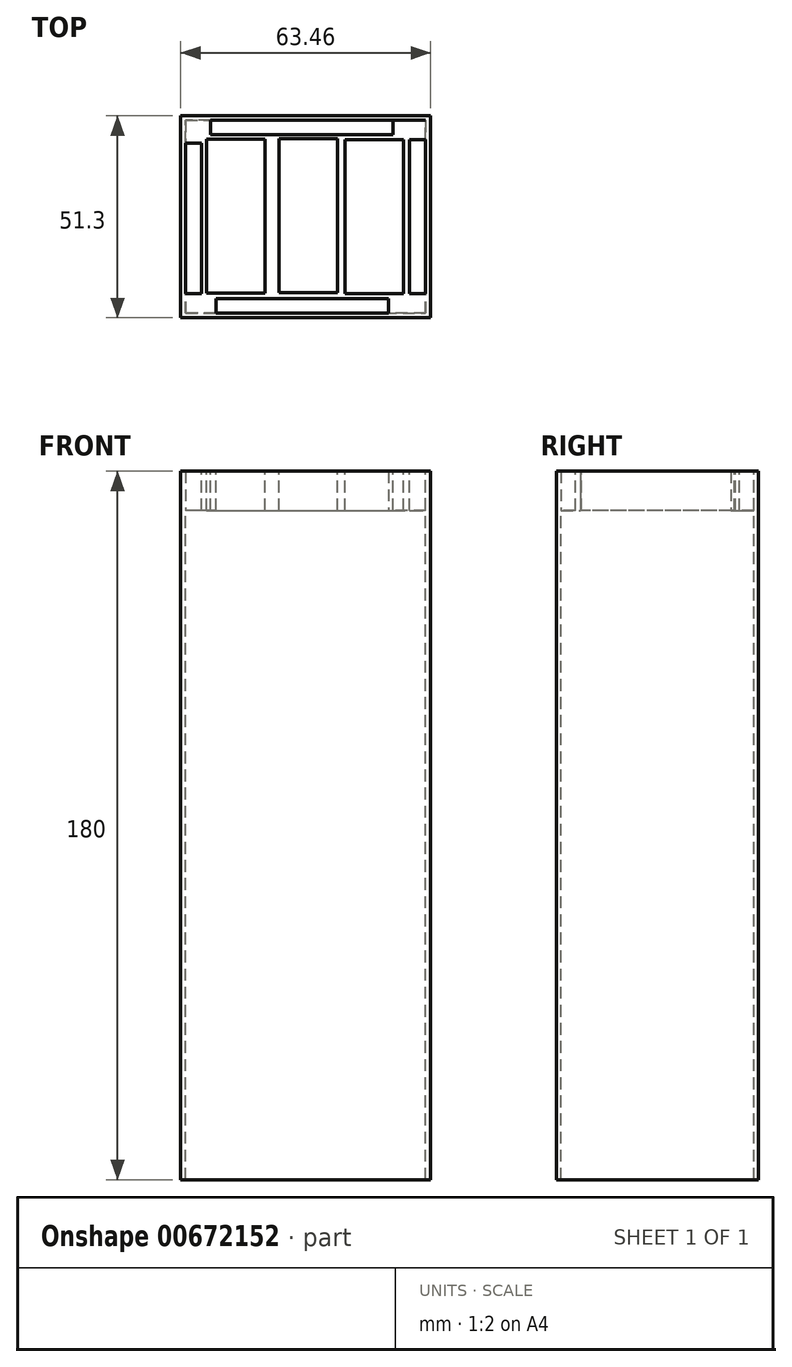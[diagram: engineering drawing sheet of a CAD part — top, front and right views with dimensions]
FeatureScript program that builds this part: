
annotation { "Feature Type Name" : "Feature", "Feature Type Description" : "" }
export const myFeature = defineFeature(function(context is Context, id is Id, definition is map)
    precondition{}
    {
        {
            var Q0;
            Q0=qCreatedBy(makeId("Top.planeOp"),FACE);
            var sketch = newSketch(context, id + "F0", { "sketchPlane" : qUnion([Q0])});
            skLineSegment(sketch, "E0.bottom", {"start": v(-30.5, 24.5) * mm, "end": v(30.5, 24.5) * mm});
            skLineSegment(sketch, "E0.top", {"start": v(-30.5, -24.5) * mm, "end": v(30.5, -24.5) * mm});
            skLineSegment(sketch, "E0.left", {"start": v(-30.5, 24.5) * mm, "end": v(-30.5, -24.5) * mm});
            skLineSegment(sketch, "E0.right", {"start": v(30.5, 24.5) * mm, "end": v(30.5, -24.5) * mm});
            skPoint(sketch, "E0.middle", {"position": v(0, 0) * mm});
            skLineSegment(sketch, "E1.bottom", {"start": v(-31.73, 25.65) * mm, "end": v(31.73, 25.65) * mm});
            skLineSegment(sketch, "E1.top", {"start": v(-31.73, -25.65) * mm, "end": v(31.73, -25.65) * mm});
            skLineSegment(sketch, "E1.left", {"start": v(-31.73, 25.65) * mm, "end": v(-31.73, -25.65) * mm});
            skLineSegment(sketch, "E1.right", {"start": v(31.73, 25.65) * mm, "end": v(31.73, -25.65) * mm});
            skSolve(sketch);
        }
        {
            var Q0;
            Q0 = qSketchRegion(id + "F0", true);
            var Q1;
            Q1 = qSketchRegion(id + "F2", true);
            extrude(context, id + "F1", {"entities" : qUnion([Q0, Q1]), "oppositeDirection" : true, "depth" : 180 * mm, "offsetDistance" : 25 * mm});
        }
        {
            var Q0;
            Q0=qCreatedBy(makeId("Front.planeOp"),FACE);
            var sketch = newSketch(context, id + "F2", { "sketchPlane" : qUnion([Q0])});
            skLineSegment(sketch, "E2", {"start": v(-37.52, 0) * mm, "end": v(-37.52, -20) * mm});
            skLineSegment(sketch, "E3", {"start": v(38.63, 0) * mm, "end": v(38.63, -20) * mm});
            skSolve(sketch);
        }
        {
            var Q0;
            Q0=qCreatedBy(makeId("Top.planeOp"),FACE);
            var sketch = newSketch(context, id + "F3", { "sketchPlane" : qUnion([Q0])});
            skLineSegment(sketch, "E4.bottom", {"start": v(-26.37, 20.82) * mm, "end": v(26.37, 20.82) * mm});
            skLineSegment(sketch, "E4.top", {"start": v(-26.37, -20.82) * mm, "end": v(26.37, -20.82) * mm});
            skLineSegment(sketch, "E4.left", {"start": v(-26.37, 20.82) * mm, "end": v(-26.37, -20.82) * mm});
            skLineSegment(sketch, "E4.right", {"start": v(26.37, 20.82) * mm, "end": v(26.37, -20.82) * mm});
            skPoint(sketch, "E4.middle", {"position": v(0, 0) * mm});
            skLineSegment(sketch, "E5.bottom", {"start": v(-25.17, 19.7) * mm, "end": v(-10.28, 19.7) * mm});
            skLineSegment(sketch, "E5.top", {"start": v(-25.17, -19.42) * mm, "end": v(-10.28, -19.42) * mm});
            skLineSegment(sketch, "E5.left", {"start": v(-25.17, 19.7) * mm, "end": v(-25.17, -19.42) * mm});
            skLineSegment(sketch, "E5.right", {"start": v(-10.28, 19.7) * mm, "end": v(-10.28, -19.42) * mm});
            skLineSegment(sketch, "E6.bottom", {"start": v(-6.78, 19.79) * mm, "end": v(8.12, 19.79) * mm});
            skLineSegment(sketch, "E6.top", {"start": v(-6.78, -19.34) * mm, "end": v(8.12, -19.34) * mm});
            skLineSegment(sketch, "E6.left", {"start": v(-6.78, 19.79) * mm, "end": v(-6.78, -19.34) * mm});
            skLineSegment(sketch, "E6.right", {"start": v(8.12, 19.79) * mm, "end": v(8.12, -19.34) * mm});
            skLineSegment(sketch, "E7.bottom", {"start": v(10.02, 19.6) * mm, "end": v(24.92, 19.6) * mm});
            skLineSegment(sketch, "E7.top", {"start": v(10.02, -19.52) * mm, "end": v(24.92, -19.52) * mm});
            skLineSegment(sketch, "E7.left", {"start": v(10.02, 19.6) * mm, "end": v(10.02, -19.52) * mm});
            skLineSegment(sketch, "E7.right", {"start": v(24.92, 19.6) * mm, "end": v(24.92, -19.52) * mm});
            skLineSegment(sketch, "E8.bottom", {"start": v(-26.37, 18.7) * mm, "end": v(-30.55, 18.7) * mm});
            skLineSegment(sketch, "E8.top", {"start": v(-26.37, 24.55) * mm, "end": v(-30.55, 24.55) * mm});
            skLineSegment(sketch, "E8.left", {"start": v(-26.37, 18.7) * mm, "end": v(-26.37, 24.55) * mm});
            skLineSegment(sketch, "E8.right", {"start": v(-30.55, 18.7) * mm, "end": v(-30.55, 24.55) * mm});
            skLineSegment(sketch, "E9.bottom", {"start": v(-24.14, 20.82) * mm, "end": v(-26.37, 20.82) * mm});
            skLineSegment(sketch, "E9.top", {"start": v(-24.14, 24.55) * mm, "end": v(-26.37, 24.55) * mm});
            skLineSegment(sketch, "E9.left", {"start": v(-24.14, 20.82) * mm, "end": v(-24.14, 24.55) * mm});
            skLineSegment(sketch, "E9.right", {"start": v(-26.37, 20.82) * mm, "end": v(-26.37, 24.55) * mm});
            skLineSegment(sketch, "E10.bottom", {"start": v(22.27, 24.49) * mm, "end": v(30.52, 24.49) * mm});
            skLineSegment(sketch, "E10.top", {"start": v(22.27, 19.6) * mm, "end": v(30.52, 19.6) * mm});
            skLineSegment(sketch, "E10.left", {"start": v(22.27, 24.49) * mm, "end": v(22.27, 19.6) * mm});
            skLineSegment(sketch, "E10.right", {"start": v(30.52, 24.49) * mm, "end": v(30.52, 19.6) * mm});
            skLineSegment(sketch, "E11.bottom", {"start": v(21.07, -19.52) * mm, "end": v(31.12, -19.52) * mm});
            skLineSegment(sketch, "E11.top", {"start": v(21.07, -24.85) * mm, "end": v(31.12, -24.85) * mm});
            skLineSegment(sketch, "E11.left", {"start": v(21.07, -19.52) * mm, "end": v(21.07, -24.85) * mm});
            skLineSegment(sketch, "E11.right", {"start": v(31.12, -19.52) * mm, "end": v(31.12, -24.85) * mm});
            skLineSegment(sketch, "E12.bottom", {"start": v(-22.78, -24.85) * mm, "end": v(-30.89, -24.85) * mm});
            skLineSegment(sketch, "E12.top", {"start": v(-22.78, -19.52) * mm, "end": v(-30.89, -19.52) * mm});
            skLineSegment(sketch, "E12.left", {"start": v(-22.78, -24.85) * mm, "end": v(-22.78, -19.52) * mm});
            skLineSegment(sketch, "E12.right", {"start": v(-30.89, -24.85) * mm, "end": v(-30.89, -19.52) * mm});
            skSolve(sketch);
        }
        {
            var Q0;
            Q0 = qSketchRegion(id + "F3", true);
            extrude(context, id + "F4", {"entities" : qUnion([Q0]), "operationType" : NewBodyOperationType.ADD, "oppositeDirection" : true, "depth" : 10 * mm, "offsetDistance" : 25 * mm});
        }
        {
            var Q0;
            Q0=sQuery(id+"F0.wireOp",EDGE,"E1.left");
            var Q1;
            Q1=sQuery(id+"F0.wireOp",EDGE,"E0.left");
            var Q2;
            Q2=sQuery(id+"F0.wireOp",EDGE,"E0.bottom");
            var Q3;
            Q3=sQuery(id+"F0.wireOp",EDGE,"E1.bottom");
            var Q4;
            Q4=sQuery(id+"F0.wireOp",EDGE,"E0.right");
            var Q5;
            Q5=sQuery(id+"F0.wireOp",EDGE,"E1.right");
            var Q6;
            Q6=sQuery(id+"F0.wireOp",EDGE,"E1.top");
            var Q7;
            Q7=sQuery(id+"F0.wireOp",EDGE,"E0.top");
            extrude(context, id + "F5", {"bodyType" : ToolBodyType.SURFACE, "surfaceEntities" : qUnion([Q0, Q1, Q2, Q3, Q4, Q5, Q6, Q7]), "depth" : 20 * mm, "offsetDistance" : 25 * mm});
        }
    });
